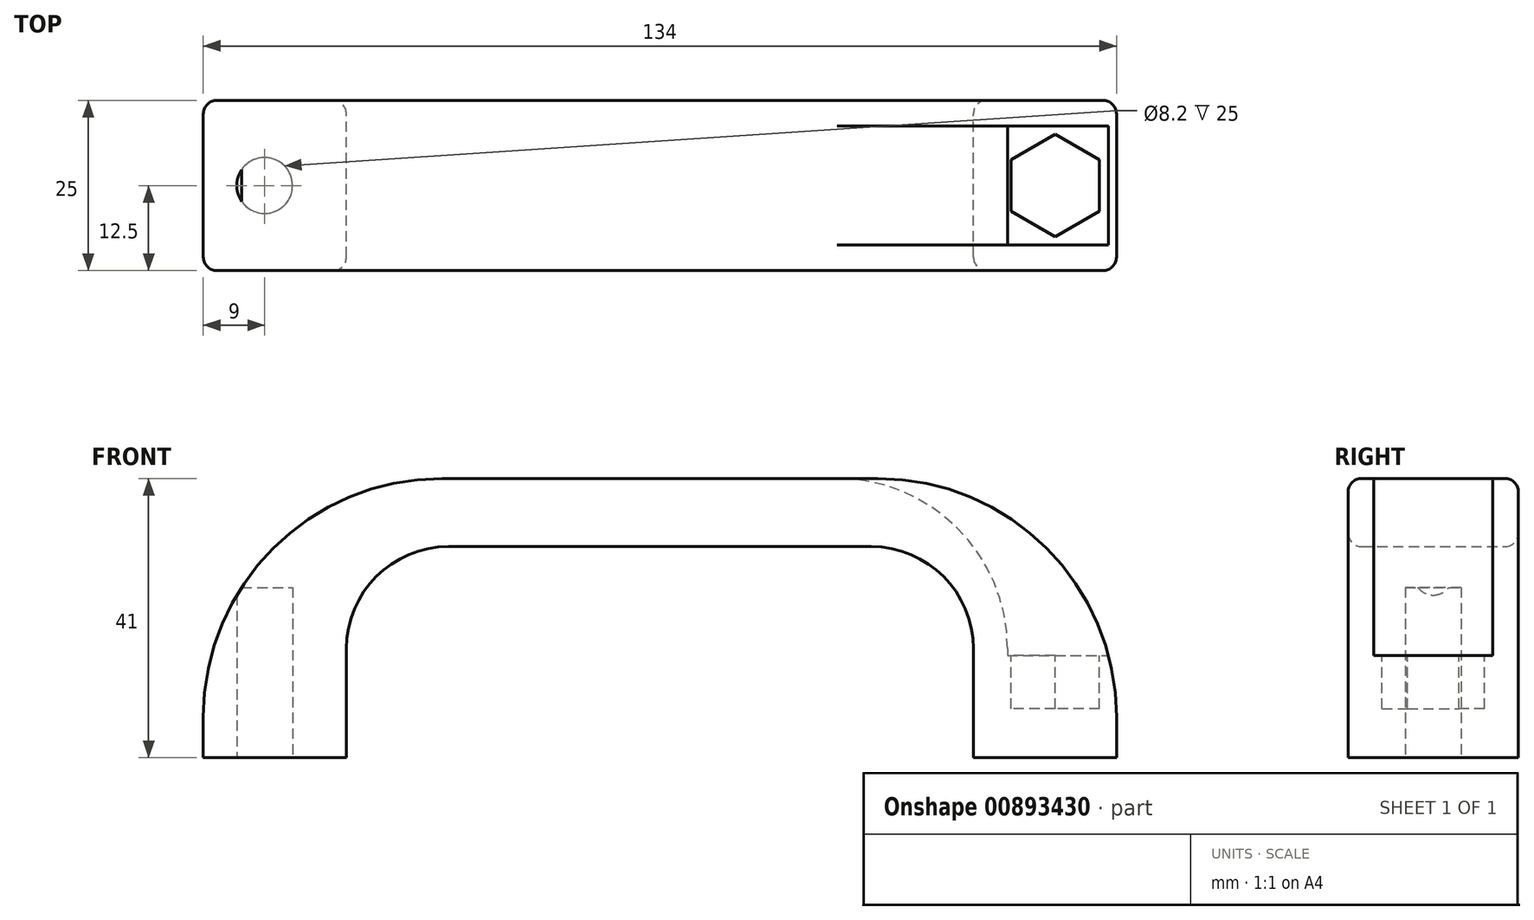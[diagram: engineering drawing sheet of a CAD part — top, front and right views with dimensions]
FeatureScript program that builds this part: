
annotation { "Feature Type Name" : "Feature", "Feature Type Description" : "" }
export const myFeature = defineFeature(function(context is Context, id is Id, definition is map)
    precondition{}
    {
        {
            var Q0;
            Q0=qCreatedBy(makeId("Front.planeOp"),FACE);
            var sketch = newSketch(context, id + "F0", { "sketchPlane" : qUnion([Q0])});
            skLineSegment(sketch, "E0", {"start": v(-67, 0) * mm, "end": v(-46, 0) * mm});
            skLineSegment(sketch, "E1", {"start": v(-46, 0) * mm, "end": v(-46, 16) * mm});
            skLineSegment(sketch, "E2", {"start": v(-31, 31) * mm, "end": v(0, 31) * mm});
            skLineSegment(sketch, "E3", {"start": v(0, 41) * mm, "end": v(-32, 41) * mm});
            skLineSegment(sketch, "E4", {"start": v(-67, 6) * mm, "end": v(-67, 0) * mm});
            skPoint(sketch, "E5.visualSharp", {"position": v(-46, 31) * mm});
            skArc(sketch, "E5.filletArc", {"start": v(-31, 31) * mm, "mid": v(-41.6, 26.6) * mm, "end": v(-46, 16) * mm});
            skPoint(sketch, "E6.visualSharp", {"position": v(-67, 41) * mm});
            skArc(sketch, "E6.filletArc", {"start": v(-32, 41) * mm, "mid": v(-56.75, 30.75) * mm, "end": v(-67, 6) * mm});
            skLineSegment(sketch, "E7.MirrorCS", {"start": v(0, 41) * mm, "end": v(32, 41) * mm});
            skArc(sketch, "E8.MirrorCS", {"start": v(32, 41) * mm, "mid": v(56.75, 30.75) * mm, "end": v(67, 6) * mm});
            skLineSegment(sketch, "E9.MirrorCS", {"start": v(67, 6) * mm, "end": v(67, 0) * mm});
            skLineSegment(sketch, "E10.MirrorCS", {"start": v(67, 0) * mm, "end": v(46, 0) * mm});
            skLineSegment(sketch, "E11.MirrorCS", {"start": v(46, 0) * mm, "end": v(46, 16) * mm});
            skArc(sketch, "E12.MirrorCS", {"start": v(31, 31) * mm, "mid": v(41.6, 26.6) * mm, "end": v(46, 16) * mm});
            skLineSegment(sketch, "E13.MirrorCS", {"start": v(31, 31) * mm, "end": v(0, 31) * mm});
            skSolve(sketch);
        }
        {
            var Q0;
            Q0=makeQuery(id+"F0.imprint","IMPRINT",FACE,{"disambiguationData":[TD([[makeQuery(id+"F0.imprint","IMPRINT",EDGE,{"derivedFrom":sQuery(id+"F0.wireOp",EDGE,"E0")}),1.0]])]});
            extrude(context, id + "F1", {"entities" : qUnion([Q0]), "depth" : 25 * mm, "offsetDistance" : 25 * mm});
        }
        {
            var Q0;
            Q0=qCreatedBy(makeId("Top.planeOp"),FACE);
            cPlane(context, id + "F2", {"entities" : qUnion([Q0]), "cplaneType" : CPlaneType.OFFSET, "offset" : 15 * mm, "width" : 150 * mm, "height" : 150 * mm});
        }
        {
            var Q0;
            Q0=qCreatedBy(id+"F2.planeOp",FACE);
            var sketch = newSketch(context, id + "F3", { "sketchPlane" : qUnion([Q0])});
            skLineSegment(sketch, "E14.bottom", {"start": v(51, -3.75) * mm, "end": v(75.13, -3.75) * mm});
            skLineSegment(sketch, "E14.top", {"start": v(51, -21.25) * mm, "end": v(75.13, -21.25) * mm});
            skLineSegment(sketch, "E14.left", {"start": v(51, -3.75) * mm, "end": v(51, -21.25) * mm});
            skLineSegment(sketch, "E14.right", {"start": v(75.13, -3.75) * mm, "end": v(75.13, -21.25) * mm});
            skSolve(sketch);
        }
        {
            var Q0;
            Q0=makeQuery(id+"F3.imprint","IMPRINT",FACE,{"disambiguationData":[TD([[makeQuery(id+"F3.imprint","IMPRINT",EDGE,{"derivedFrom":sQuery(id+"F3.wireOp",EDGE,"E14.bottom")}),-1.0]])]});
            extrude(context, id + "F4", {"entities" : qUnion([Q0]), "operationType" : NewBodyOperationType.REMOVE, "depth" : 25 * mm, "offsetDistance" : 25 * mm});
        }
        {
            var Q0;
            Q0=makeQuery(id+"F4.boolean.opBoolean","INTERSECT",EDGE,{"derivedFrom":[makeQuery(id+"F1.opExtrude","SWEPT_FACE",FACE,{"disambiguationData":[OSD([sQuery(id+"F0.wireOp",EDGE,"E8.MirrorCS")])]}),makeQuery(id+"F4.opExtrude","SWEPT_FACE",FACE,{"disambiguationData":[OSD([sQuery(id+"F3.wireOp",EDGE,"E14.left")])]})]});
            fillet(context, id + "F5", {"entities" : qUnion([Q0]), "radius" : 25 * mm, "tangentPropagation" : true, "allowEdgeOverflow" : false});
        }
        {
            var Q0;
            Q0=makeQuery(id+"F3.imprint","IMPRINT",FACE,{"disambiguationData":[TD([[makeQuery(id+"F3.imprint","IMPRINT",EDGE,{"derivedFrom":sQuery(id+"F3.wireOp",EDGE,"E14.bottom")}),-1.0]])]});
            var sketch = newSketch(context, id + "F6", { "sketchPlane" : qUnion([Q0])});
            skCircle(sketch, "E15.cCircle", {"center": v(58, -12.5) * mm, "radius": 6.5 * mm, "construction": true});
            skLineSegment(sketch, "E15.0", {"start": v(51.5, -16.25) * mm, "end": v(51.5, -8.75) * mm});
            skLineSegment(sketch, "E15.1", {"start": v(51.5, -8.75) * mm, "end": v(58, -5) * mm});
            skLineSegment(sketch, "E15.2", {"start": v(58, -5) * mm, "end": v(64.5, -8.75) * mm});
            skLineSegment(sketch, "E15.3", {"start": v(64.5, -8.75) * mm, "end": v(64.5, -16.25) * mm});
            skLineSegment(sketch, "E15.4", {"start": v(64.5, -16.25) * mm, "end": v(58, -20) * mm});
            skLineSegment(sketch, "E15.5", {"start": v(58, -20) * mm, "end": v(51.5, -16.25) * mm});
            skPoint(sketch, "E15.0.midPoint", {"position": v(51.5, -12.5) * mm});
            skSolve(sketch);
        }
        {
            var Q0;
            Q0=makeQuery(id+"F6.imprint","IMPRINT",FACE,{"disambiguationData":[TD([[makeQuery(id+"F6.imprint","IMPRINT",EDGE,{"derivedFrom":sQuery(id+"F6.wireOp",EDGE,"E15.0")}),-1.0]])]});
            extrude(context, id + "F7", {"entities" : qUnion([Q0]), "operationType" : NewBodyOperationType.REMOVE, "oppositeDirection" : true, "depth" : 7.8 * mm, "offsetDistance" : 25 * mm});
        }
        {
            var Q0;
            Q0=makeQuery(id+"F1.opExtrude","SWEPT_FACE",FACE,{"disambiguationData":[OSD([sQuery(id+"F0.wireOp",EDGE,"E0")])]});
            var sketch = newSketch(context, id + "F8", { "sketchPlane" : qUnion([Q0])});
            skCircle(sketch, "E16", {"center": v(-58, 12.5) * mm, "radius": 4.1 * mm});
            skSolve(sketch);
        }
        {
            var Q0;
            Q0=makeQuery(id+"F8.imprint","IMPRINT",FACE,{"disambiguationData":[TD([[makeQuery(id+"F8.imprint","IMPRINT",EDGE,{"derivedFrom":sQuery(id+"F8.wireOp",EDGE,"E16")}),1.0]])]});
            extrude(context, id + "F9", {"entities" : qUnion([Q0]), "operationType" : NewBodyOperationType.REMOVE, "oppositeDirection" : true, "depth" : 25 * mm, "offsetDistance" : 25 * mm});
        }
        {
            var Q0;
            Q0=makeQuery(id+"F1.opExtrude","CAP_EDGE",EDGE,{"disambiguationData":[OSD([sQuery(id+"F0.wireOp",EDGE,"E6.filletArc")])],"isStart":false});
            var Q1;
            Q1=makeQuery(id+"F1.opExtrude","CAP_EDGE",EDGE,{"disambiguationData":[OSD([sQuery(id+"F0.wireOp",EDGE,"E2"),sQuery(id+"F0.wireOp",EDGE,"E13.MirrorCS")])],"isStart":false});
            var Q2;
            Q2=makeQuery(id+"F1.opExtrude","CAP_EDGE",EDGE,{"disambiguationData":[OSD([sQuery(id+"F0.wireOp",EDGE,"E6.filletArc")])],"isStart":true});
            var Q3;
            Q3=makeQuery(id+"F1.opExtrude","CAP_EDGE",EDGE,{"disambiguationData":[OSD([sQuery(id+"F0.wireOp",EDGE,"E2"),sQuery(id+"F0.wireOp",EDGE,"E13.MirrorCS")])],"isStart":true});
            fillet(context, id + "F10", {"entities" : qUnion([Q0, Q1, Q2, Q3]), "radius" : 2 * mm, "tangentPropagation" : true, "allowEdgeOverflow" : false});
        }
    });
